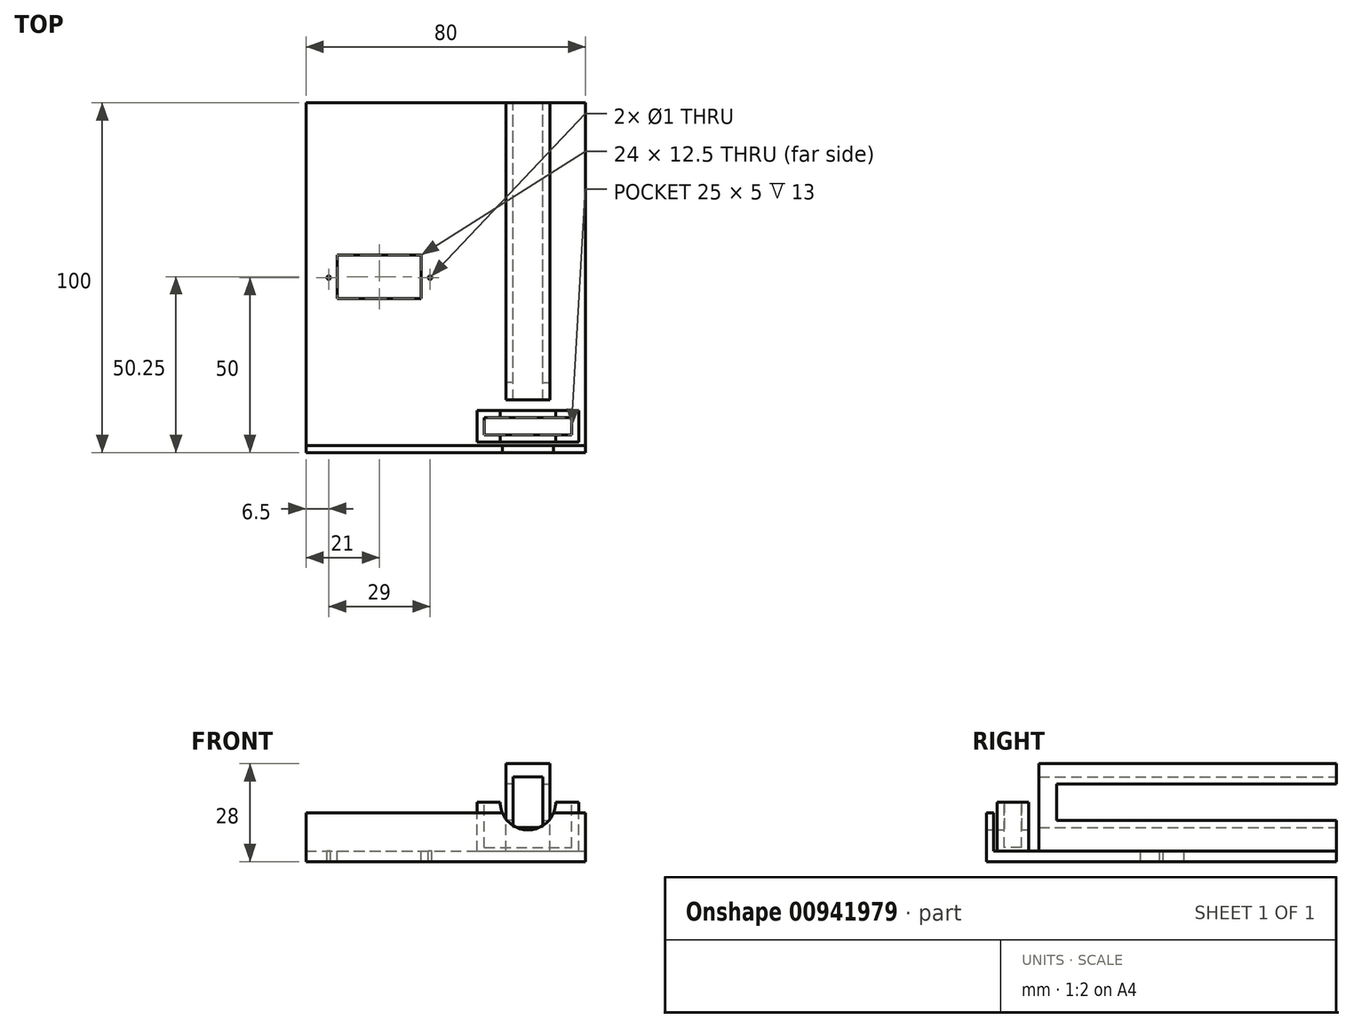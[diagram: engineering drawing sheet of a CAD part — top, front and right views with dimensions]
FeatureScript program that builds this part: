
annotation { "Feature Type Name" : "Feature", "Feature Type Description" : "" }
export const myFeature = defineFeature(function(context is Context, id is Id, definition is map)
    precondition{}
    {
        {
            var Q0;
            Q0=qCreatedBy(makeId("Top.planeOp"),FACE);
            var sketch = newSketch(context, id + "F0", { "sketchPlane" : qUnion([Q0])});
            skLineSegment(sketch, "E0.bottom", {"start": v(0, 0) * mm, "end": v(80, 0) * mm});
            skLineSegment(sketch, "E0.top", {"start": v(0, 100) * mm, "end": v(80, 100) * mm});
            skLineSegment(sketch, "E0.left", {"start": v(0, 0) * mm, "end": v(0, 100) * mm});
            skLineSegment(sketch, "E0.right", {"start": v(80, 0) * mm, "end": v(80, 100) * mm});
            skSolve(sketch);
        }
        {
            var Q0;
            Q0=makeQuery(id+"F0.imprint","IMPRINT",FACE,{"disambiguationData":[TD([[makeQuery(id+"F0.imprint","IMPRINT",EDGE,{"derivedFrom":sQuery(id+"F0.wireOp",EDGE,"E0.bottom")}),1.0]])]});
            extrude(context, id + "F1", {"entities" : qUnion([Q0]), "depth" : 34 * mm, "offsetDistance" : 25 * mm});
        }
        {
            var Q0;
            Q0=makeQuery(id+"F1.opExtrude","CAP_FACE",FACE,{"disambiguationData":[OSD([sQuery(id+"F0.wireOp",EDGE,"E0.bottom"),sQuery(id+"F0.wireOp",EDGE,"E0.top"),sQuery(id+"F0.wireOp",EDGE,"E0.left"),sQuery(id+"F0.wireOp",EDGE,"E0.right")])],"isStart":false});
            var sketch = newSketch(context, id + "F2", { "sketchPlane" : qUnion([Q0])});
            skLineSegment(sketch, "E1.bottom", {"start": v(9, 44) * mm, "end": v(33, 44) * mm});
            skLineSegment(sketch, "E1.top", {"start": v(9, 56.5) * mm, "end": v(33, 56.5) * mm});
            skLineSegment(sketch, "E1.left", {"start": v(9, 44) * mm, "end": v(9, 56.5) * mm});
            skLineSegment(sketch, "E1.right", {"start": v(33, 44) * mm, "end": v(33, 56.5) * mm});
            skLineSegment(sketch, "E2.bottom", {"start": v(51, 10) * mm, "end": v(76, 10) * mm});
            skLineSegment(sketch, "E2.top", {"start": v(51, 5) * mm, "end": v(76, 5) * mm});
            skLineSegment(sketch, "E2.left", {"start": v(51, 10) * mm, "end": v(51, 5) * mm});
            skLineSegment(sketch, "E2.right", {"start": v(76, 10) * mm, "end": v(76, 5) * mm});
            skLineSegment(sketch, "E3.bottom", {"start": v(3, 42) * mm, "end": v(39, 42) * mm});
            skLineSegment(sketch, "E3.top", {"start": v(3, 58.5) * mm, "end": v(39, 58.5) * mm});
            skLineSegment(sketch, "E3.left", {"start": v(3, 42) * mm, "end": v(3, 58.5) * mm});
            skLineSegment(sketch, "E3.right", {"start": v(39, 42) * mm, "end": v(39, 58.5) * mm});
            skLineSegment(sketch, "E4.bottom", {"start": v(49, 12) * mm, "end": v(78, 12) * mm});
            skLineSegment(sketch, "E4.top", {"start": v(49, 3) * mm, "end": v(78, 3) * mm});
            skLineSegment(sketch, "E4.left", {"start": v(49, 12) * mm, "end": v(49, 3) * mm});
            skLineSegment(sketch, "E4.right", {"start": v(78, 12) * mm, "end": v(78, 3) * mm});
            skLineSegment(sketch, "E5.bottom", {"start": v(57.25, 100) * mm, "end": v(69.75, 100) * mm});
            skLineSegment(sketch, "E5.top", {"start": v(57.25, 15) * mm, "end": v(69.75, 15) * mm});
            skLineSegment(sketch, "E5.left", {"start": v(57.25, 100) * mm, "end": v(57.25, 15) * mm});
            skLineSegment(sketch, "E5.right", {"start": v(69.75, 100) * mm, "end": v(69.75, 15) * mm});
            skCircle(sketch, "E6", {"center": v(35.5, 50) * mm, "radius": 0.5 * mm});
            skCircle(sketch, "E7", {"center": v(6.5, 50) * mm, "radius": 0.5 * mm});
            skLineSegment(sketch, "E8.bottom", {"start": v(0, 0) * mm, "end": v(80, 0) * mm});
            skLineSegment(sketch, "E8.top", {"start": v(0, 2) * mm, "end": v(80, 2) * mm});
            skLineSegment(sketch, "E8.left", {"start": v(0, 0) * mm, "end": v(0, 2) * mm});
            skLineSegment(sketch, "E8.right", {"start": v(80, 0) * mm, "end": v(80, 2) * mm});
            skSolve(sketch);
        }
        {
            var Q0;
            Q0=makeQuery(id+"F1.opExtrude","SWEPT_FACE",FACE,{"disambiguationData":[OSD([sQuery(id+"F0.wireOp",EDGE,"E0.top")])]});
            var sketch = newSketch(context, id + "F3", { "sketchPlane" : qUnion([Q0])});
            skLineSegment(sketch, "E9.bottom", {"start": v(-67.75, 9.75) * mm, "end": v(-59.25, 9.75) * mm});
            skLineSegment(sketch, "E9.top", {"start": v(-67.75, 24.25) * mm, "end": v(-59.25, 24.25) * mm});
            skLineSegment(sketch, "E9.left", {"start": v(-67.75, 9.75) * mm, "end": v(-67.75, 24.25) * mm});
            skLineSegment(sketch, "E9.right", {"start": v(-59.25, 9.75) * mm, "end": v(-59.25, 24.25) * mm});
            skLineSegment(sketch, "E10.bottom", {"start": v(-59.25, 11.75) * mm, "end": v(-57.25, 11.75) * mm});
            skLineSegment(sketch, "E10.top", {"start": v(-59.25, 22.25) * mm, "end": v(-57.25, 22.25) * mm});
            skLineSegment(sketch, "E10.left", {"start": v(-59.25, 11.75) * mm, "end": v(-59.25, 22.25) * mm});
            skLineSegment(sketch, "E10.right", {"start": v(-57.25, 11.75) * mm, "end": v(-57.25, 22.25) * mm});
            skLineSegment(sketch, "E11.bottom", {"start": v(-67.75, 11.75) * mm, "end": v(-69.75, 11.75) * mm});
            skLineSegment(sketch, "E11.top", {"start": v(-67.75, 22.25) * mm, "end": v(-69.75, 22.25) * mm});
            skLineSegment(sketch, "E11.left", {"start": v(-67.75, 11.75) * mm, "end": v(-67.75, 22.25) * mm});
            skLineSegment(sketch, "E11.right", {"start": v(-69.75, 11.75) * mm, "end": v(-69.75, 22.25) * mm});
            skSolve(sketch);
        }
        {
            var Q0;
            Q0=makeQuery(id+"F2.imprint","IMPRINT",FACE,{"disambiguationData":[TD([[makeQuery(id+"F2.imprint","IMPRINT",EDGE,{"derivedFrom":sQuery(id+"F2.wireOp",EDGE,"E3.bottom")}),-1.0]])]});
            extrude(context, id + "F4", {"entities" : qUnion([Q0]), "operationType" : NewBodyOperationType.REMOVE, "oppositeDirection" : true, "depth" : 31 * mm, "offsetDistance" : 25 * mm});
        }
        {
            var Q0;
            Q0=makeQuery(id+"F3.imprint","IMPRINT",FACE,{"disambiguationData":[TD([[makeQuery(id+"F3.imprint","IMPRINT",EDGE,{"derivedFrom":sQuery(id+"F3.wireOp",EDGE,"E9.bottom")}),1.0]])]});
            extrude(context, id + "F5", {"entities" : qUnion([Q0]), "operationType" : NewBodyOperationType.REMOVE, "oppositeDirection" : true, "depth" : 85 * mm, "offsetDistance" : 25 * mm});
        }
        {
            var Q0;
            Q0=makeQuery(id+"F3.imprint","IMPRINT",FACE,{"disambiguationData":[TD([[makeQuery(id+"F3.imprint","IMPRINT",EDGE,{"derivedFrom":sQuery(id+"F3.wireOp",EDGE,"E10.bottom")}),1.0]])]});
            var Q1;
            Q1=makeQuery(id+"F3.imprint","IMPRINT",FACE,{"disambiguationData":[TD([[makeQuery(id+"F3.imprint","IMPRINT",EDGE,{"derivedFrom":sQuery(id+"F3.wireOp",EDGE,"E11.bottom")}),-1.0]])]});
            extrude(context, id + "F6", {"entities" : qUnion([Q0, Q1]), "operationType" : NewBodyOperationType.REMOVE, "oppositeDirection" : true, "depth" : 80 * mm, "offsetDistance" : 25 * mm});
        }
        {
            var Q0;
            Q0=makeQuery(id+"F2.imprint","IMPRINT",FACE,{"disambiguationData":[TD([[makeQuery(id+"F2.imprint","IMPRINT",EDGE,{"derivedFrom":sQuery(id+"F2.wireOp",EDGE,"E1.bottom")}),1.0]])]});
            var Q1;
            Q1=makeQuery(id+"F2.imprint","IMPRINT",FACE,{"disambiguationData":[TD([[makeQuery(id+"F2.imprint","IMPRINT",EDGE,{"derivedFrom":sQuery(id+"F2.wireOp",EDGE,"E7")}),1.0]])]});
            var Q2;
            Q2=makeQuery(id+"F2.imprint","IMPRINT",FACE,{"disambiguationData":[TD([[makeQuery(id+"F2.imprint","IMPRINT",EDGE,{"derivedFrom":sQuery(id+"F2.wireOp",EDGE,"E6")}),1.0]])]});
            extrude(context, id + "F7", {"entities" : qUnion([Q0, Q1, Q2]), "operationType" : NewBodyOperationType.REMOVE, "oppositeDirection" : true, "depth" : 37 * mm, "offsetDistance" : 25 * mm});
        }
        {
            var Q0;
            Q0=makeQuery(id+"F2.imprint","IMPRINT",FACE,{"disambiguationData":[TD([[makeQuery(id+"F2.imprint","IMPRINT",EDGE,{"derivedFrom":sQuery(id+"F2.wireOp",EDGE,"E1.bottom")}),-1.0]])]});
            extrude(context, id + "F8", {"entities" : qUnion([Q0]), "operationType" : NewBodyOperationType.REMOVE, "oppositeDirection" : true, "depth" : 31 * mm, "offsetDistance" : 25 * mm});
        }
        {
            var Q0;
            Q0=makeQuery(id+"F2.imprint","IMPRINT",FACE,{"disambiguationData":[TD([[makeQuery(id+"F2.imprint","IMPRINT",EDGE,{"derivedFrom":sQuery(id+"F2.wireOp",EDGE,"E2.bottom")}),-1.0]])]});
            extrude(context, id + "F9", {"entities" : qUnion([Q0]), "operationType" : NewBodyOperationType.REMOVE, "oppositeDirection" : true, "depth" : 30 * mm, "offsetDistance" : 25 * mm});
        }
        {
            var Q0;
            Q0=makeQuery(id+"F2.imprint","IMPRINT",FACE,{"disambiguationData":[TD([[makeQuery(id+"F2.imprint","IMPRINT",EDGE,{"derivedFrom":sQuery(id+"F2.wireOp",EDGE,"E2.bottom")}),1.0]])]});
            extrude(context, id + "F10", {"entities" : qUnion([Q0]), "operationType" : NewBodyOperationType.REMOVE, "oppositeDirection" : true, "depth" : 17 * mm, "offsetDistance" : 25 * mm});
        }
        {
            var Q0;
            Q0=makeQuery(id+"F4.boolean.opBoolean","COPY",FACE,{"derivedFrom":makeQuery(id+"F4.opExtrude","SWEPT_FACE",FACE,{"disambiguationData":[OSD([sQuery(id+"F2.wireOp",EDGE,"E4.bottom")])]})});
            var sketch = newSketch(context, id + "F11", { "sketchPlane" : qUnion([Q0])});
            skCircle(sketch, "E12", {"center": v(-63.5, 17) * mm, "radius": 7.93 * mm});
            skSolve(sketch);
        }
        {
            var Q0;
            {var subQ0=sQuery(id+"F11.wireOp",EDGE,"E12");var subQ1=makeQuery(id+"F10.boolean.opBoolean","COPY",EDGE,{"derivedFrom":makeQuery(id+"F10.opExtrude","CAP_EDGE",EDGE,{"disambiguationData":[OSD([sQuery(id+"F2.wireOp",EDGE,"E4.bottom")])],"isStart":false})});var subQ2=makeQuery(id+"F11.imprint","INTERSECT",VERTEX,{"disambiguationData":[OD(0.0)],"derivedFrom":[subQ1,subQ0]});Q0=makeQuery(id+"F11.imprint","IMPRINT",FACE,{"disambiguationData":[TD([[makeQuery(id+"F11.imprint","IMPRINT",EDGE,{"disambiguationData":[TD([[subQ2,1.0]])],"derivedFrom":subQ0}),1.0]])]});}
            extrude(context, id + "F12", {"entities" : qUnion([Q0]), "operationType" : NewBodyOperationType.REMOVE, "oppositeDirection" : true, "depth" : 15 * mm, "offsetDistance" : 25 * mm});
        }
        {
            var Q0;
            {var subQ0=sQuery(id+"F0.wireOp",EDGE,"E0.top");Q0=makeQuery(id+"F4.boolean.opBoolean","SPLIT",FACE,{"disambiguationData":[TD([makeQuery(id+"F1.opExtrude","SWEPT_FACE",FACE,{"disambiguationData":[OSD([subQ0])]})])],"derivedFrom":makeQuery(id+"F1.opExtrude","CAP_FACE",FACE,{"disambiguationData":[OSD([sQuery(id+"F0.wireOp",EDGE,"E0.bottom"),subQ0,sQuery(id+"F0.wireOp",EDGE,"E0.left"),sQuery(id+"F0.wireOp",EDGE,"E0.right")])],"isStart":false})});}
            extrude(context, id + "F13", {"entities" : qUnion([Q0]), "operationType" : NewBodyOperationType.REMOVE, "oppositeDirection" : true, "depth" : 6 * mm, "offsetDistance" : 25 * mm});
        }
        {
            var Q0;
            {var subQ0=sQuery(id+"F0.wireOp",EDGE,"E0.bottom");var subQ1=sQuery(id+"F0.wireOp",EDGE,"E0.right");var subQ2=sQuery(id+"F0.wireOp",EDGE,"E0.left");Q0=makeQuery(id+"F4.boolean.opBoolean","SPLIT",FACE,{"disambiguationData":[TD([makeQuery(id+"F1.opExtrude","SWEPT_FACE",FACE,{"disambiguationData":[OSD([subQ0])]})])],"derivedFrom":makeQuery(id+"F1.opExtrude","CAP_FACE",FACE,{"disambiguationData":[OSD([subQ0,sQuery(id+"F0.wireOp",EDGE,"E0.top"),subQ2,subQ1])],"isStart":false})});}
            extrude(context, id + "F14", {"entities" : qUnion([Q0]), "operationType" : NewBodyOperationType.REMOVE, "oppositeDirection" : true, "depth" : 20 * mm, "offsetDistance" : 25 * mm});
        }
    });
